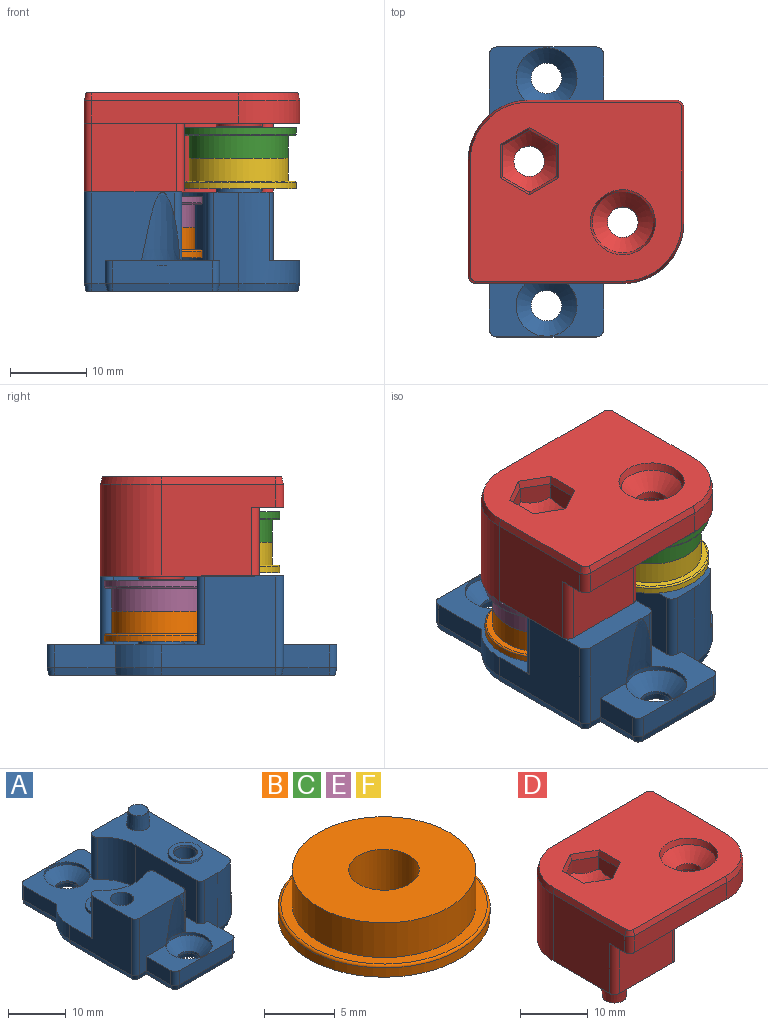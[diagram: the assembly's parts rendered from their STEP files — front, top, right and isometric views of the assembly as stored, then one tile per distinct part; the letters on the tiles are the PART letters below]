
ASSEMBLY  parts=6 mates=5
PART A: 97 faces, bbox 28.3x38x16 mm
  f0: plane 38x17.77mm, normal (0,0,1), area 331.5mm2, adj f11,f12,f13,f14,f16,f17,f18,f21
  f1: plane 24x12.11mm, normal (0,0,1), area 178.3mm2, adj f13,f14,f19,f21,f24,f25,f27,f28
  f2: plane 0.31x0.18mm, normal (0,0,-1), area 0mm2, adj f50,f51,f54
  f3: plane 0.36x0.1mm, normal (0,0,-1), area 0mm2, adj f51,f52,f54
  f4: plane 0.31x0.18mm, normal (0,0,-1), area 0mm2, adj f47,f52,f54
  f5: plane 0.31x0.18mm, normal (0,0,-1), area 0mm2, adj f47,f48,f54
  f6: plane 0.36x0.1mm, normal (0,0,-1), area 0mm2, adj f48,f49,f54
  f7: cylinder r=2mm len=7.8mm, axis (0,0,-1), area 98mm2, adj f54,f91
  f8: cylinder r=2mm len=4mm, axis (0,0,-1), area 12.6mm2, adj f46,f94
  f9: cylinder r=2mm len=4mm, axis (0,0,-1), area 5mm2, adj f44,f71
  f10: cylinder r=2mm len=4mm, axis (0,0,-1), area 5mm2, adj f45,f70
  f11: plane 12x10.8mm, normal (0,-1,0), area 74.5mm2, adj f0,f12,f22,f31,f39,f41,f89
  f12: cylinder r=1mm len=9mm, axis (0,0,-1), area 11.5mm2, adj f0,f11,f22,f23,f41
  f13: plane 12x3.27mm, normal (0,-1,0), area 36.9mm2, adj f0,f1,f19,f29,f38,f80
  f14: plane 13.61x12mm, normal (0,1,0), area 119.5mm2, adj f0,f1,f26,f27,f30,f34,f35,f72
  f15: plane 15x3mm, normal (1,0,0), area 45mm2, adj f19,f26,f30,f76
  f16: cylinder r=8mm len=9.6mm, axis (0,0,-1), area 95.5mm2, adj f0,f22,f32,f33
  f17: cylinder r=8mm len=6.05mm, axis (0,0,-1), area 20.6mm2, adj f0,f18,f37,f83
  f18: plane 15x12mm, normal (-1,0,0), area 129.1mm2, adj f0,f17,f22,f31,f33,f85
  f19: cylinder r=8mm len=12mm, axis (0,0,-1), area 75.4mm2, adj f1,f13,f15,f26,f28,f78
  f20: plane 37.46x27.73mm, normal (0,0,-1), area 689.6mm2, adj f63,f64,f65,f66,f67,f68,f69,f70
  f21: cylinder r=8mm len=9mm, axis (0,0,-1), area 64.2mm2, adj f0,f1,f24,f34
  f22: plane 12.8x11.34mm, normal (0,0,1), area 102.5mm2, adj f11,f12,f16,f18,f23,f31,f32,f33
  f23: plane 9x6.84mm, normal (1,0,0), area 61.6mm2, adj f0,f12,f22,f32
  f24: plane 15x9mm, normal (-1,0,0), area 135mm2, adj f0,f1,f21,f29
  f25: plane 21.06x9mm, normal (1,0,0), area 189.6mm2, adj f1,f26,f27,f28
  f26: plane 22.93x4.5mm, normal (0,0,1), area 72.3mm2, adj f14,f15,f19,f25,f27,f28,f30
  f27: cylinder r=1mm len=9mm, axis (0,0,-1), area 14.1mm2, adj f1,f14,f25,f26
  f28: cylinder r=1mm len=9mm, axis (0,0,-1), area 9.4mm2, adj f1,f19,f25,f26
  f29: cylinder r=1mm len=9mm, axis (0,0,-1), area 14.1mm2, adj f0,f1,f13,f24
  f30: cylinder r=1mm len=3mm, axis (0,0,1), area 4.7mm2, adj f14,f15,f26,f74
  f31: cylinder r=1mm len=12mm, axis (0,0,1), area 18.8mm2, adj f11,f18,f22,f87
  f32: cylinder r=1mm len=9mm, axis (0,0,-1), area 18.1mm2, adj f0,f16,f22,f23
  f33: cylinder r=1mm len=9mm, axis (0,0,-1), area 22.2mm2, adj f0,f16,f18,f22
  f34: cylinder r=1mm len=9mm, axis (0,0,-1), area 22.2mm2, adj f0,f1,f14,f21
  f35: plane 6x3mm, normal (1,0,0), area 18mm2, adj f0,f14,f62,f73
  f36: plane 13x3mm, normal (0,1,0), area 39mm2, adj f0,f61,f62,f77
  f37: plane 7.95x3mm, normal (-1,0,0), area 23.9mm2, adj f0,f17,f61,f81
  f38: plane 6x3mm, normal (1,0,0), area 18mm2, adj f0,f13,f60,f82
  f39: plane 6x3mm, normal (-1,0,0), area 18mm2, adj f0,f11,f59,f90
  f40: plane 13x3mm, normal (0,-1,0), area 39mm2, adj f0,f59,f60,f86
  f41: cone r=4mm half-angle=7deg, axis (0,0,-1), area 32.2mm2, adj f11,f12,f43
  f42: cylinder r=4mm len=8mm, axis (0,0,1), area 15.1mm2, adj f0,f45
  f43: cylinder r=4mm len=8mm, axis (0,0,1), area 15.1mm2, adj f0,f41,f44
  f44: cone r=2mm half-angle=45deg, axis (0,0,1), area 53.3mm2, adj f9,f43
  f45: cone r=4mm half-angle=45deg, axis (0,0,1), area 53.3mm2, adj f10,f42
  f46: cone r=4mm half-angle=45deg, axis (0,0,-1), area 53.3mm2, adj f8,f63
  f47: plane 4.1x2.65mm, normal (1,0,0), area 10.1mm2, adj f4,f5,f48,f52,f54,f68
  f48: plane 3.55x2.65mm, normal (0.5,0.87,0), area 10.1mm2, adj f5,f6,f47,f49,f54,f69
  f49: plane 3.55x2.65mm, normal (-0.5,0.87,0), area 10.1mm2, adj f6,f48,f50,f53,f54,f67
  f50: plane 4.1x2.65mm, normal (-1,0,0), area 10.1mm2, adj f2,f49,f51,f53,f54,f65
  f51: plane 3.55x2.65mm, normal (-0.5,-0.87,0), area 10.1mm2, adj f2,f3,f50,f52,f54,f64
  f52: plane 3.55x2.65mm, normal (0.5,-0.87,0), area 10.1mm2, adj f3,f4,f47,f51,f54,f66
  f53: plane 0.31x0.18mm, normal (0,0,-1), area 0mm2, adj f49,f50,f54
  f54: cone r=4mm half-angle=45deg, axis (0,0,-1), area 43.8mm2, adj f2,f3,f4,f5,f6,f7,f47,f48
  f55: cone r=2mm half-angle=3deg, axis (0,0,1), area 38.6mm2, adj f22,f56
  f56: plane 3.66x3.66mm, normal (0,0,1), area 10.5mm2, adj f55
  f57: cone r=2mm half-angle=5deg, axis (0,0,-1), area 35.4mm2, adj f1,f58
  f58: plane 3.48x3.48mm, normal (0,0,1), area 9.5mm2, adj f57
  f59: cylinder r=1mm len=3mm, axis (0,0,1), area 4.7mm2, adj f0,f39,f40,f88
  f60: cylinder r=1mm len=3mm, axis (0,0,-1), area 4.7mm2, adj f0,f38,f40,f84
  f61: cylinder r=1mm len=3mm, axis (0,0,-1), area 4.7mm2, adj f0,f36,f37,f79
  f62: cylinder r=1mm len=3mm, axis (0,0,1), area 4.7mm2, adj f0,f35,f36,f75
  f63: cone r=4mm half-angle=15deg, axis (0,0,-1), area 26.9mm2, adj f20,f46
  f64: plane 3.82x2.36mm, normal (-0.48,-0.84,-0.26), area 4.4mm2, adj f20,f51,f65,f66
  f65: plane 4.41x1mm, normal (-0.97,0,-0.26), area 4.4mm2, adj f20,f50,f64,f67
  f66: plane 3.82x2.36mm, normal (0.48,-0.84,-0.26), area 4.4mm2, adj f20,f52,f64,f68
  f67: plane 3.82x2.36mm, normal (-0.48,0.84,-0.26), area 4.4mm2, adj f20,f49,f65,f69
  f68: plane 4.41x1mm, normal (0.97,0,-0.26), area 4.4mm2, adj f20,f47,f66,f69
  f69: plane 3.82x2.36mm, normal (0.48,0.84,-0.26), area 4.4mm2, adj f20,f48,f67,f68
  f70: cone r=2mm half-angle=15deg, axis (0,0,-1), area 13.9mm2, adj f10,f20
  f71: cone r=2.27mm half-angle=15deg, axis (0,0,-1), area 13.9mm2, adj f9,f20
  f72: plane 9.77x1mm, normal (0,0.97,-0.26), area 10mm2, adj f14,f20,f73,f74
  f73: plane 6.27x1mm, normal (0.97,0,-0.26), area 6.4mm2, adj f20,f35,f72,f75
  f74: cone r=0.73mm half-angle=15deg, axis (0,0,1), area 1.4mm2, adj f20,f30,f72,f76
  f75: cone r=0.73mm half-angle=15deg, axis (0,0,1), area 1.4mm2, adj f20,f62,f73,f77
  f76: plane 15x1mm, normal (0.97,0,-0.26), area 15.5mm2, adj f15,f20,f74,f78
  f77: plane 13x1mm, normal (0,0.97,-0.26), area 13.5mm2, adj f20,f36,f75,f79
  f78: cone r=7.73mm half-angle=15deg, axis (0,0,1), area 12.8mm2, adj f19,f20,f76,f80
  f79: cone r=0.73mm half-angle=15deg, axis (0,0,1), area 1.4mm2, adj f20,f61,f77,f81
  f80: plane 2.77x1mm, normal (0,-0.97,-0.26), area 2.7mm2, adj f13,f20,f78,f82
  f81: plane 8.08x1mm, normal (-0.97,0,-0.26), area 8.3mm2, adj f20,f37,f79,f83
  f82: plane 6.27x1mm, normal (0.97,0,-0.26), area 6.4mm2, adj f20,f38,f80,f84
  f83: cone r=7.73mm half-angle=15deg, axis (0,0,1), area 7mm2, adj f17,f20,f81,f85
  f84: cone r=0.73mm half-angle=15deg, axis (0,0,1), area 1.4mm2, adj f20,f60,f82,f86
  f85: plane 15x1mm, normal (-0.97,0,-0.26), area 15.5mm2, adj f18,f20,f83,f87
  f86: plane 13x1mm, normal (0,-0.97,-0.26), area 13.5mm2, adj f20,f40,f84,f88
  f87: cone r=0.73mm half-angle=15deg, axis (0,0,1), area 1.4mm2, adj f20,f31,f85,f89
  f88: cone r=0.73mm half-angle=15deg, axis (0,0,1), area 1.4mm2, adj f20,f59,f86,f90
  f89: plane 2.03x1mm, normal (0,-0.97,-0.26), area 2mm2, adj f11,f20,f87,f90
  f90: plane 6.27x1mm, normal (-0.97,0,-0.26), area 6.4mm2, adj f20,f39,f88,f89
  f91: cone r=2mm half-angle=10deg, axis (0,0,1), area 5.2mm2, adj f7,f93
  f92: cone r=3mm half-angle=10deg, axis (0,0,-1), area 7.6mm2, adj f1,f93
  f93: plane 5.86x5.86mm, normal (0,0,1), area 13.5mm2, adj f91,f92
  f94: cone r=2mm half-angle=10deg, axis (0,0,1), area 5.2mm2, adj f8,f96
  f95: cone r=3mm half-angle=10deg, axis (0,0,-1), area 7.6mm2, adj f0,f96
  f96: plane 5.86x5.86mm, normal (0,0,1), area 13.5mm2, adj f94,f95
PART B: 7 faces, bbox 16.2x16.2x4 mm
  f0: cylinder r=2.5mm len=5mm, axis (0,0,-1), area 62.8mm2, adj f3,f5
  f1: cylinder r=7.5mm len=15mm, axis (0,0,-1), area 37.7mm2, adj f3,f6
  f2: plane 14.6x14.6mm, normal (0,0,1), area 34.7mm2, adj f4,f6
  f3: plane 15x15mm, normal (0,0,-1), area 157.1mm2, adj f0,f1
  f4: cylinder r=6.5mm len=13mm, axis (0,0,-1), area 122.5mm2, adj f2,f5
  f5: plane 13x13mm, normal (0,0,1), area 113.1mm2, adj f0,f4
  f6: torus R=7.3mm, axis (0,0,1), area 14.7mm2, adj f1,f2
PART C: same geometry as B
PART D: 59 faces, bbox 28.3x24x16 mm
  f0: plane 28.27x24mm, normal (0,0,-1), area 264.3mm2, adj f9,f10,f12,f14,f15,f16,f17,f18
  f1: plane 24.77x20.8mm, normal (0,0,-1), area 304.5mm2, adj f9,f10,f11,f12,f14,f15,f20,f21
  f2: plane 0.31x0.18mm, normal (0,0,1), area 0mm2, adj f29,f30,f33
  f3: plane 0.36x0.1mm, normal (0,0,1), area 0mm2, adj f30,f31,f33
  f4: plane 0.31x0.18mm, normal (0,0,1), area 0mm2, adj f31,f32,f33
  f5: plane 0.31x0.18mm, normal (0,0,1), area 0mm2, adj f27,f32,f33
  f6: plane 0.36x0.1mm, normal (0,0,1), area 0mm2, adj f27,f28,f33
  f7: plane 27.73x23.46mm, normal (0,0,1), area 517mm2, adj f38,f39,f40,f41,f42,f43,f44,f45
  f8: cylinder r=2mm len=4mm, axis (0,0,-1), area 12.6mm2, adj f25,f56
  f9: cylinder r=8mm len=11.38mm, axis (0,0,-1), area 173.2mm2, adj f0,f1,f21,f22
  f10: plane 19.27x12mm, normal (0,1,0), area 199.7mm2, adj f0,f1,f11,f23,f24,f48
  f11: cylinder r=8mm len=12mm, axis (0,0,-1), area 150.8mm2, adj f1,f10,f12,f50
  f12: plane 15x12mm, normal (-1,0,0), area 151.2mm2, adj f0,f1,f11,f19,f20,f52
  f13: cylinder r=2mm len=7.8mm, axis (0,0,-1), area 98mm2, adj f33,f53
  f14: plane 9x6.71mm, normal (1,0,0), area 60.4mm2, adj f0,f1,f22,f24
  f15: plane 11.11x9mm, normal (0,-1,0), area 100mm2, adj f0,f1,f20,f21
  f16: plane 19.27x3mm, normal (0,-1,0), area 57.8mm2, adj f0,f17,f19,f49
  f17: cylinder r=8mm len=8mm, axis (0,0,-1), area 37.7mm2, adj f0,f16,f18,f47
  f18: plane 15x3mm, normal (1,0,0), area 45mm2, adj f0,f17,f23,f45
  f19: cylinder r=1mm len=3mm, axis (0,0,1), area 4.7mm2, adj f0,f12,f16,f51
  f20: cylinder r=1mm len=9mm, axis (0,0,1), area 14.1mm2, adj f0,f1,f12,f15
  f21: cylinder r=1mm len=9mm, axis (0,0,-1), area 18.1mm2, adj f0,f1,f9,f15
  f22: cylinder r=1mm len=9mm, axis (0,0,-1), area 17.7mm2, adj f0,f1,f9,f14
  f23: cylinder r=1mm len=3mm, axis (0,0,1), area 4.7mm2, adj f0,f10,f18,f46
  f24: cylinder r=1mm len=9mm, axis (0,0,-1), area 14.1mm2, adj f0,f1,f10,f14
  f25: cone r=4mm half-angle=45deg, axis (0,0,1), area 53.3mm2, adj f8,f38
  f26: plane 0.31x0.18mm, normal (0,0,1), area 0mm2, adj f28,f29,f33
  f27: plane 3.55x2.65mm, normal (0.5,-0.87,0), area 10.1mm2, adj f5,f6,f28,f32,f33,f41
  f28: plane 3.55x2.65mm, normal (-0.5,-0.87,0), area 10.1mm2, adj f6,f26,f27,f29,f33,f39
  f29: plane 4.1x2.65mm, normal (-1,0,0), area 10.1mm2, adj f2,f26,f28,f30,f33,f40
  f30: plane 3.55x2.65mm, normal (-0.5,0.87,0), area 10.1mm2, adj f2,f3,f29,f31,f33,f42
  f31: plane 3.55x2.65mm, normal (0.5,0.87,0), area 10.1mm2, adj f3,f4,f30,f32,f33,f44
  f32: plane 4.1x2.65mm, normal (1,0,0), area 10.1mm2, adj f4,f5,f27,f31,f33,f43
  f33: cone r=2mm half-angle=45deg, axis (0,0,1), area 43.8mm2, adj f2,f3,f4,f5,f6,f13,f26,f27
  f34: cone r=2mm half-angle=3deg, axis (0,0,-1), area 38.6mm2, adj f1,f35
  f35: plane 3.66x3.66mm, normal (0,0,-1), area 10.5mm2, adj f34
  f36: cone r=2mm half-angle=5deg, axis (0,0,1), area 35.4mm2, adj f1,f37
  f37: plane 3.48x3.48mm, normal (0,0,-1), area 9.5mm2, adj f36
  f38: cone r=4mm half-angle=15deg, axis (0,0,1), area 26.9mm2, adj f7,f25
  f39: plane 3.82x2.36mm, normal (-0.48,-0.84,0.26), area 4.4mm2, adj f7,f28,f40,f41
  f40: plane 4.41x1mm, normal (-0.97,0,0.26), area 4.4mm2, adj f7,f29,f39,f42
  f41: plane 3.82x2.36mm, normal (0.48,-0.84,0.26), area 4.4mm2, adj f7,f27,f39,f43
  f42: plane 3.82x2.36mm, normal (-0.48,0.84,0.26), area 4.4mm2, adj f7,f30,f40,f44
  f43: plane 4.41x1mm, normal (0.97,0,0.26), area 4.4mm2, adj f7,f32,f41,f44
  f44: plane 3.82x2.36mm, normal (0.48,0.84,0.26), area 4.4mm2, adj f7,f31,f42,f43
  f45: plane 15x1mm, normal (0.97,0,0.26), area 15.5mm2, adj f7,f18,f46,f47
  f46: cone r=0.73mm half-angle=15deg, axis (0,0,-1), area 1.4mm2, adj f7,f23,f45,f48
  f47: cone r=8mm half-angle=15deg, axis (0,0,-1), area 12.8mm2, adj f7,f17,f45,f49
  f48: plane 19.27x1mm, normal (0,0.97,0.26), area 19.9mm2, adj f7,f10,f46,f50
  f49: plane 19.27x1mm, normal (0,-0.97,0.26), area 19.9mm2, adj f7,f16,f47,f51
  f50: cone r=8mm half-angle=15deg, axis (0,0,-1), area 12.8mm2, adj f7,f11,f48,f52
  f51: cone r=0.73mm half-angle=15deg, axis (0,0,-1), area 1.4mm2, adj f7,f19,f49,f52
  f52: plane 15x1mm, normal (-0.97,0,0.26), area 15.5mm2, adj f7,f12,f50,f51
  f53: cone r=2mm half-angle=10deg, axis (0,0,-1), area 5.2mm2, adj f13,f55
  f54: cone r=3mm half-angle=10deg, axis (0,0,1), area 7.6mm2, adj f1,f55
  f55: plane 5.86x5.86mm, normal (0,0,-1), area 13.5mm2, adj f53,f54
  f56: cone r=2mm half-angle=10deg, axis (0,0,-1), area 5.2mm2, adj f8,f58
  f57: cone r=3mm half-angle=10deg, axis (0,0,1), area 7.6mm2, adj f0,f58
  f58: plane 5.86x5.86mm, normal (0,0,-1), area 13.5mm2, adj f56,f57
PART E: same geometry as B
PART F: same geometry as B
PLACE A rot(axis=(-0.21,0,0.98),0deg) t=(0.47,0.86,-13.48)mm
PLACE B t=(-5.66,4.86,-9.08)mm
PLACE C rot(axis=(1,0,0),180deg) t=(6.61,-3.14,7.92)mm
PLACE D t=(0.47,0.86,-13.48)mm
PLACE E rot(axis=(-1,0,0),180deg) t=(-5.66,4.86,-1.08)mm
PLACE F t=(6.61,-3.14,-0.08)mm
MATE fastened A.f7 <-> F.f0  axis (0,0,1) through (6.61,-3.14,-0.08)mm
MATE fastened A.f8 <-> B.f0  axis (0,0,1) through (-5.66,4.86,-9.08)mm
MATE fastened B.f0 <-> E.f0  axis (0,0,1) through (-5.66,4.86,-5.08)mm
MATE fastened F.f0 <-> C.f0  axis (0,0,1) through (6.61,-3.14,3.92)mm
MATE fastened A.f57 <-> D.f34  axis (0,0,1) through (7.11,8.86,-0.48)mm
